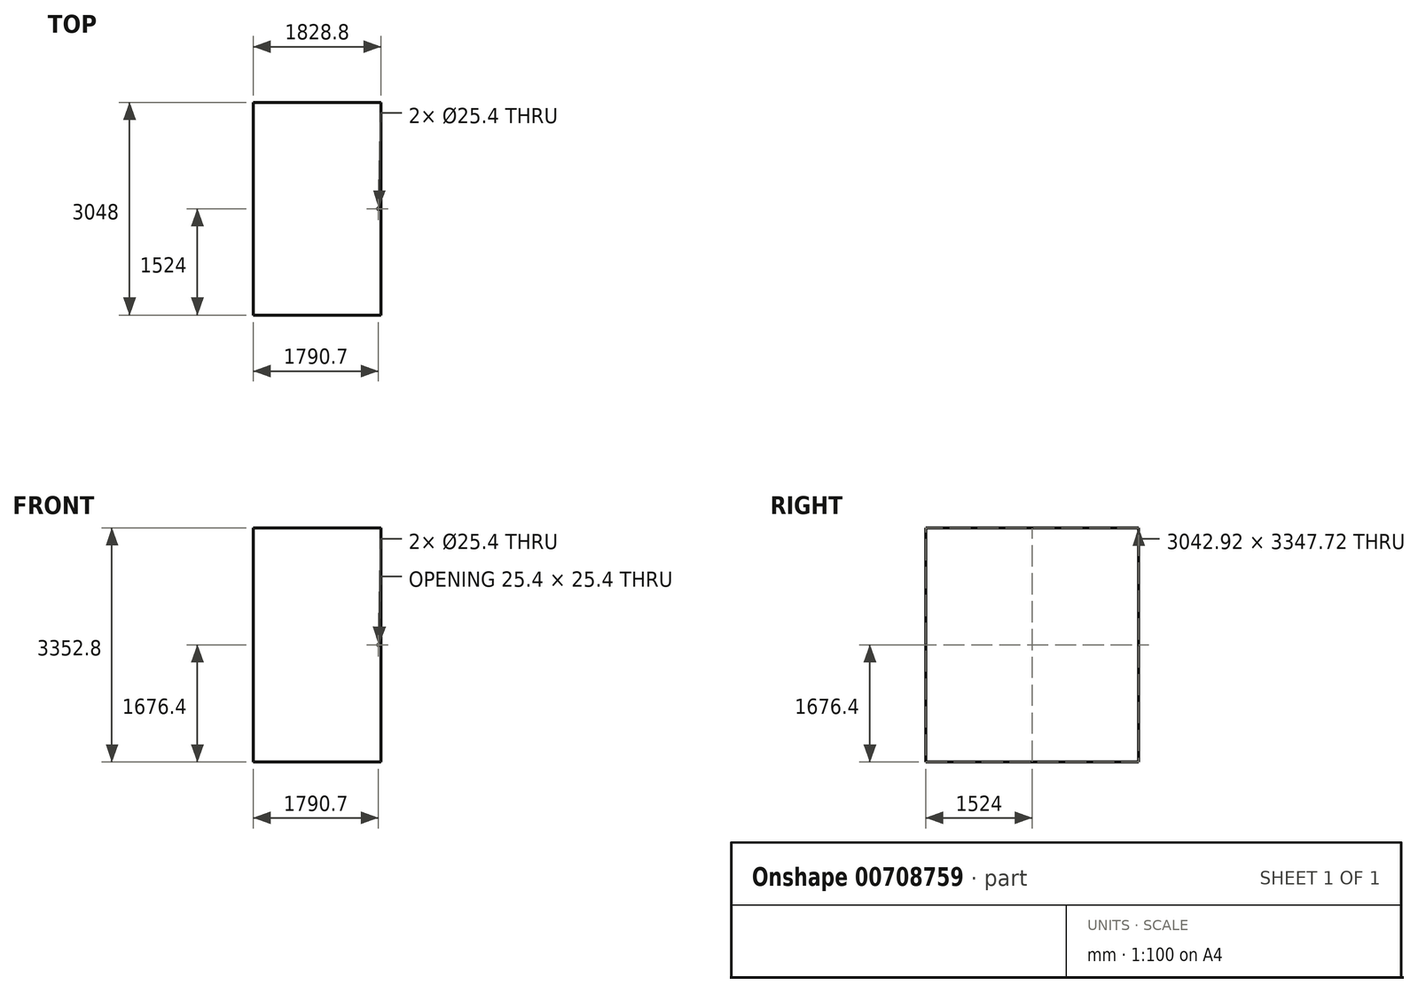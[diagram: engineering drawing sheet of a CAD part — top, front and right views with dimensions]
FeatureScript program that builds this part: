
annotation { "Feature Type Name" : "Feature", "Feature Type Description" : "" }
export const myFeature = defineFeature(function(context is Context, id is Id, definition is map)
    precondition{}
    {
        {
            var Q0;
            Q0=qCreatedBy(makeId("Front.planeOp"),FACE);
            var sketch = newSketch(context, id + "F0", { "sketchPlane" : qUnion([Q0])});
            skLineSegment(sketch, "E0", {"start": v(0, 0) * mm, "end": v(0, 3352.8) * mm});
            skLineSegment(sketch, "E1", {"start": v(0, 3352.8) * mm, "end": v(1828.8, 3352.8) * mm});
            skLineSegment(sketch, "E2", {"start": v(1828.8, 3352.8) * mm, "end": v(1828.8, 0) * mm});
            skLineSegment(sketch, "E3", {"start": v(1828.8, 0) * mm, "end": v(0, 0) * mm});
            skSolve(sketch);
        }
        {
            var Q0;
            Q0 = qSketchRegion(id + "F0", true);
            extrude(context, id + "F1", {"entities" : qUnion([Q0]), "depth" : 3048 * mm, "offsetDistance" : 25.4 * mm});
        }
        {
            var Q0;
            Q0=makeQuery(id+"F1.opExtrude","SWEPT_FACE",FACE,{"disambiguationData":[OSD([sQuery(id+"F0.wireOp",EDGE,"E2")])]});
            var sketch = newSketch(context, id + "F2", { "sketchPlane" : qUnion([Q0])});
            skLineSegment(sketch, "E4.bottom", {"start": v(-3045.46, 2.54) * mm, "end": v(-2.54, 2.54) * mm});
            skLineSegment(sketch, "E4.top", {"start": v(-3045.46, 3350.26) * mm, "end": v(-2.54, 3350.26) * mm});
            skLineSegment(sketch, "E4.left", {"start": v(-3045.46, 2.54) * mm, "end": v(-3045.46, 3350.26) * mm});
            skLineSegment(sketch, "E4.right", {"start": v(-2.54, 2.54) * mm, "end": v(-2.54, 3350.26) * mm});
            skSolve(sketch);
        }
        {
            var Q0;
            Q0 = qSketchRegion(id + "F2", true);
            extrude(context, id + "F3", {"entities" : qUnion([Q0]), "operationType" : NewBodyOperationType.REMOVE, "endBound" : BoundingType.UP_TO_NEXT, "oppositeDirection" : true, "depth" : 25.4 * mm, "offsetDistance" : 25.4 * mm});
        }
        {
            var Q0;
            Q0=makeQuery(id+"F1.opExtrude","CAP_FACE",FACE,{"disambiguationData":[OSD([sQuery(id+"F0.wireOp",EDGE,"E0"),sQuery(id+"F0.wireOp",EDGE,"E1"),sQuery(id+"F0.wireOp",EDGE,"E2"),sQuery(id+"F0.wireOp",EDGE,"E3")])],"isStart":false});
            var sketch = newSketch(context, id + "F4", { "sketchPlane" : qUnion([Q0])});
            skPoint(sketch, "E5", {"position": v(1790.7, 1676.4) * mm});
            skSolve(sketch);
        }
        {
            var Q0;
            Q0=sQuery(id+"F4.wireOp",VERTEX,"E5");
            var Q1;
            Q1=makeQuery(id+"F1.opExtrude","SWEPT_BODY",BODY,{"disambiguationData":[OSD([sQuery(id+"F0.wireOp",EDGE,"E0"),sQuery(id+"F0.wireOp",EDGE,"E1"),sQuery(id+"F0.wireOp",EDGE,"E2"),sQuery(id+"F0.wireOp",EDGE,"E3")])]});
            hole(context, id + "F5", {"style" : HoleStyle.SIMPLE, "endStyle" : HoleEndStyle.THROUGH, "holeDiameter" : 25.4 * mm, "majorDiameter" : 6.35 * mm, "isTappedThrough" : true, "tappedDepth" : 12.7 * mm, "tapClearance" : 3, "locations" : qUnion([Q0]), "scope" : qUnion([Q1])});
        }
        {
            var Q0;
            Q0=makeQuery(id+"F1.opExtrude","SWEPT_FACE",FACE,{"disambiguationData":[OSD([sQuery(id+"F0.wireOp",EDGE,"E1")])]});
            var sketch = newSketch(context, id + "F6", { "sketchPlane" : qUnion([Q0])});
            skPoint(sketch, "E6", {"position": v(1790.7, -1524) * mm});
            skSolve(sketch);
        }
        {
            var Q0;
            Q0=sQuery(id+"F6.wireOp",VERTEX,"E6");
            var Q1;
            Q1=makeQuery(id+"F1.opExtrude","SWEPT_BODY",BODY,{"disambiguationData":[OSD([sQuery(id+"F0.wireOp",EDGE,"E0"),sQuery(id+"F0.wireOp",EDGE,"E1"),sQuery(id+"F0.wireOp",EDGE,"E2"),sQuery(id+"F0.wireOp",EDGE,"E3")])]});
            hole(context, id + "F7", {"style" : HoleStyle.SIMPLE, "endStyle" : HoleEndStyle.THROUGH, "holeDiameter" : 25.4 * mm, "majorDiameter" : 6.35 * mm, "isTappedThrough" : true, "tappedDepth" : 12.7 * mm, "tapClearance" : 3, "locations" : qUnion([Q0]), "scope" : qUnion([Q1])});
        }
    });
